FREECAD ASSEMBLY — COMPONENT RECIPES ("01_assembly_frame")

This assembly document has 7 components, labeled P0..P6 below (a component is one placed body or linked part). 0 of them carry a construction recipe — the FreeCAD feature program that regenerates the part from scratch, quoted from this document or its linked companion documents; the rest are supplied as boundary geometry only. No exploded tour is included for this assembly.
COMPONENT P0 — geometry summary ("Body"; no construction recipe available for this part):
  bounding box: 594.0 x 450.0 x 30.0 mm
  tessellated surface: 8,912 triangles
  volume: 896561 mm^3 (11% of its bounding box)
COMPONENT P1 — geometry summary ("Body001"; no construction recipe available for this part):
  bounding box: 15.0 x 10.0 x 10.0 mm
  tessellated surface: 708 triangles
  volume: 1086 mm^3 (72% of its bounding box)
  symmetry: revolution-symmetric about the y axis through its bounding-box center; mirror-symmetric across its x mid-plane, z mid-plane
COMPONENT P2 — geometry summary ("Body002"; no construction recipe available for this part):
  bounding box: 15.0 x 10.0 x 10.0 mm
  tessellated surface: 708 triangles
  volume: 1086 mm^3 (72% of its bounding box)
  symmetry: revolution-symmetric about the y axis through its bounding-box center; mirror-symmetric across its x mid-plane, z mid-plane
COMPONENT P3 — geometry summary ("Body003"; no construction recipe available for this part):
  bounding box: 15.0 x 10.0 x 10.0 mm
  tessellated surface: 708 triangles
  volume: 1086 mm^3 (72% of its bounding box)
  symmetry: revolution-symmetric about the y axis through its bounding-box center; mirror-symmetric across its x mid-plane, z mid-plane
COMPONENT P4 — geometry summary ("Body004"; no construction recipe available for this part):
  bounding box: 15.0 x 10.0 x 10.0 mm
  tessellated surface: 708 triangles
  volume: 1086 mm^3 (72% of its bounding box)
  symmetry: revolution-symmetric about the y axis through its bounding-box center; mirror-symmetric across its x mid-plane, z mid-plane
COMPONENT P5 — geometry summary ("Body005"; no construction recipe available for this part):
  bounding box: 15.0 x 10.0 x 10.0 mm
  tessellated surface: 708 triangles
  volume: 1086 mm^3 (72% of its bounding box)
  symmetry: revolution-symmetric about the y axis through its bounding-box center; mirror-symmetric across its x mid-plane, z mid-plane
COMPONENT P6 — geometry summary ("Body006"; no construction recipe available for this part):
  bounding box: 15.0 x 10.0 x 10.0 mm
  tessellated surface: 708 triangles
  volume: 1086 mm^3 (72% of its bounding box)
  symmetry: revolution-symmetric about the y axis through its bounding-box center; mirror-symmetric across its x mid-plane, z mid-plane
PROVENANCE & LICENSES
A FreeCAD (.FCStd) document from a public repository crawl; recipes are the document's own serialized feature recipes (and, for linked parts, companion documents' recipes).
License: as declared in the source repository (recorded in the dataset sidecar).
